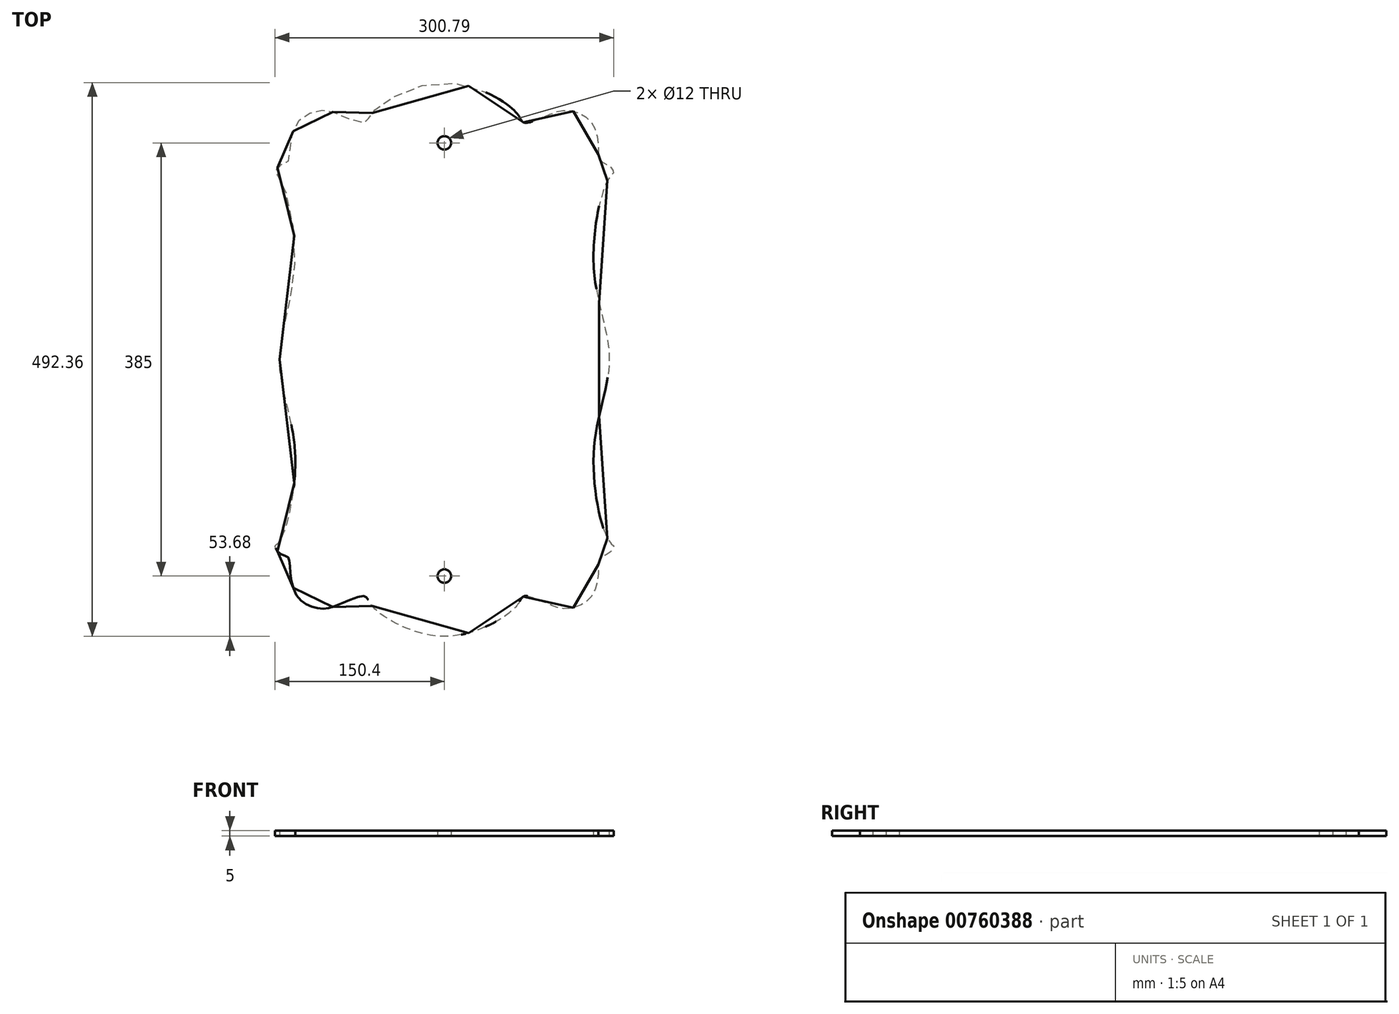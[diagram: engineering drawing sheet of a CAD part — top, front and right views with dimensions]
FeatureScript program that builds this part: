
annotation { "Feature Type Name" : "Feature", "Feature Type Description" : "" }
export const myFeature = defineFeature(function(context is Context, id is Id, definition is map)
    precondition{}
    {
        {
            var Q0;
            Q0=qCreatedBy(makeId("Top.planeOp"),FACE);
            var sketch = newSketch(context, id + "F0", { "sketchPlane" : qUnion([Q0])});
            skPoint(sketch, "E0", {"position": v(150.32, -165.76) * mm});
            skPoint(sketch, "E1", {"position": v(107.37, -221.56) * mm});
            skPoint(sketch, "E2", {"position": v(69.02, -211.72) * mm});
            skPoint(sketch, "E3", {"position": v(0, -246.18) * mm});
            skPoint(sketch, "E4", {"position": v(138.05, -177.25) * mm});
            skPoint(sketch, "E5", {"position": v(146.48, 0) * mm});
            skPoint(sketch, "E6", {"position": v(132.68, -82.88) * mm});
            skLineSegment(sketch, "E7", {"start": v(0, 292) * mm, "end": v(0, -246.18) * mm, "construction": true});
            skPoint(sketch, "E8.MirrorP", {"position": v(-146.48, 0) * mm});
            skPoint(sketch, "E9.MirrorP", {"position": v(-132.68, -82.88) * mm});
            skPoint(sketch, "E10.MirrorP", {"position": v(-150.32, -165.76) * mm});
            skPoint(sketch, "E11.MirrorP", {"position": v(-138.05, -177.25) * mm});
            skPoint(sketch, "E12.MirrorP", {"position": v(-107.37, -221.56) * mm});
            skPoint(sketch, "E13.MirrorP", {"position": v(-69.02, -211.72) * mm});
            skPoint(sketch, "E14", {"position": v(0, 0) * mm});
            skPoint(sketch, "E15", {"position": v(-146.25, -161.4) * mm});
            skPoint(sketch, "E16", {"position": v(-136.87, -189.28) * mm});
            skPoint(sketch, "E17", {"position": v(-146.26, -172.33) * mm});
            skPoint(sketch, "E18", {"position": v(-131.04, -210.06) * mm});
            skPoint(sketch, "E19", {"position": v(-94.82, -218.38) * mm});
            skPoint(sketch, "E20", {"position": v(-60.59, -222.84) * mm});
            skPoint(sketch, "E21", {"position": v(-67.25, -214.49) * mm});
            skPoint(sketch, "E22", {"position": v(-72.48, -210.2) * mm});
            skPoint(sketch, "E23", {"position": v(-119.37, -219.05) * mm});
            skPoint(sketch, "E24", {"position": v(-149.89, -167.68) * mm});
            skPoint(sketch, "E25.MirrorP", {"position": v(60.59, -222.84) * mm});
            skPoint(sketch, "E26.MirrorP", {"position": v(67.25, -214.49) * mm});
            skPoint(sketch, "E27.MirrorP", {"position": v(72.48, -210.2) * mm});
            skPoint(sketch, "E28.MirrorP", {"position": v(94.82, -218.38) * mm});
            skPoint(sketch, "E29.MirrorP", {"position": v(119.37, -219.05) * mm});
            skPoint(sketch, "E30.MirrorP", {"position": v(136.87, -189.28) * mm});
            skPoint(sketch, "E31.MirrorP", {"position": v(146.26, -172.33) * mm});
            skPoint(sketch, "E32.MirrorP", {"position": v(149.89, -167.68) * mm});
            skPoint(sketch, "E33.MirrorP", {"position": v(146.25, -161.4) * mm});
            skPoint(sketch, "E34", {"position": v(-139.73, -175.31) * mm});
            skPoint(sketch, "E35.MirrorP", {"position": v(131.04, -210.06) * mm});
            skPoint(sketch, "E36.MirrorP", {"position": v(-132.68, 82.88) * mm});
            skPoint(sketch, "E37.MirrorP", {"position": v(-139.73, 175.31) * mm});
            skPoint(sketch, "E38.MirrorP", {"position": v(-150.32, 165.76) * mm});
            skPoint(sketch, "E39.MirrorP", {"position": v(69.02, 211.72) * mm});
            skPoint(sketch, "E40.MirrorP", {"position": v(150.32, 165.76) * mm});
            skPoint(sketch, "E41.MirrorP", {"position": v(-67.25, 214.49) * mm});
            skPoint(sketch, "E42.MirrorP", {"position": v(131.04, 210.06) * mm});
            skPoint(sketch, "E43.MirrorP", {"position": v(60.59, 222.84) * mm});
            skPoint(sketch, "E44.MirrorP", {"position": v(119.37, 219.05) * mm});
            skPoint(sketch, "E45.MirrorP", {"position": v(136.87, 189.28) * mm});
            skPoint(sketch, "E46.MirrorP", {"position": v(-72.48, 210.2) * mm});
            skPoint(sketch, "E47.MirrorP", {"position": v(-138.05, 177.25) * mm});
            skPoint(sketch, "E48.MirrorP", {"position": v(-69.02, 211.72) * mm});
            skPoint(sketch, "E49.MirrorP", {"position": v(72.48, 210.2) * mm});
            skPoint(sketch, "E50.MirrorP", {"position": v(-146.25, 161.4) * mm});
            skPoint(sketch, "E51.MirrorP", {"position": v(-136.87, 189.28) * mm});
            skPoint(sketch, "E52.MirrorP", {"position": v(138.05, 177.25) * mm});
            skPoint(sketch, "E53.MirrorP", {"position": v(67.25, 214.49) * mm});
            skPoint(sketch, "E54.MirrorP", {"position": v(-149.89, 167.68) * mm});
            skPoint(sketch, "E55.MirrorP", {"position": v(149.89, 167.68) * mm});
            skPoint(sketch, "E56.MirrorP", {"position": v(-107.37, 221.56) * mm});
            skPoint(sketch, "E57.MirrorP", {"position": v(-94.82, 218.38) * mm});
            skPoint(sketch, "E58.MirrorP", {"position": v(146.26, 172.33) * mm});
            skPoint(sketch, "E59.MirrorP", {"position": v(107.37, 221.56) * mm});
            skPoint(sketch, "E60.MirrorP", {"position": v(-131.04, 210.06) * mm});
            skPoint(sketch, "E61.MirrorP", {"position": v(94.82, 218.38) * mm});
            skPoint(sketch, "E62.MirrorP", {"position": v(146.25, 161.4) * mm});
            skPoint(sketch, "E63.MirrorP", {"position": v(0, 246.18) * mm});
            skPoint(sketch, "E64.MirrorP", {"position": v(-146.26, 172.33) * mm});
            skPoint(sketch, "E65.MirrorP", {"position": v(-119.37, 219.05) * mm});
            skPoint(sketch, "E66.MirrorP", {"position": v(-60.59, 222.84) * mm});
            skPoint(sketch, "E67.MirrorP", {"position": v(132.68, 82.88) * mm});
            skFitSpline(sketch, "E68", {"points": [v(-146.48, 0) * mm, v(-132.68, 82.88) * mm, v(-146.25, 161.4) * mm, v(-150.32, 165.76) * mm, v(-149.89, 167.68) * mm, v(-146.26, 172.33) * mm, v(-139.73, 175.31) * mm, v(-138.05, 177.25) * mm, v(-136.87, 189.28) * mm, v(-131.04, 210.06) * mm, v(-119.37, 219.05) * mm, v(-107.37, 221.56) * mm, v(-94.82, 218.38) * mm, v(-72.48, 210.2) * mm, v(-69.02, 211.72) * mm, v(-67.25, 214.49) * mm, v(-60.59, 222.84) * mm, v(0, 246.18) * mm, v(60.59, 222.84) * mm, v(67.25, 214.49) * mm, v(69.02, 211.72) * mm, v(72.48, 210.2) * mm, v(94.82, 218.38) * mm, v(107.37, 221.56) * mm, v(119.37, 219.05) * mm, v(131.04, 210.06) * mm, v(136.87, 189.28) * mm, v(138.05, 177.25) * mm, v(146.26, 172.33) * mm, v(149.89, 167.68) * mm, v(150.32, 165.76) * mm, v(146.25, 161.4) * mm, v(132.68, 82.88) * mm, v(146.48, 0) * mm, v(132.68, -82.88) * mm, v(146.25, -161.4) * mm, v(150.32, -165.76) * mm, v(149.89, -167.68) * mm, v(146.26, -172.33) * mm, v(138.05, -177.25) * mm, v(136.87, -189.28) * mm, v(131.04, -210.06) * mm, v(119.37, -219.05) * mm, v(107.37, -221.56) * mm, v(94.82, -218.38) * mm, v(72.48, -210.2) * mm, v(69.02, -211.72) * mm, v(67.25, -214.49) * mm, v(60.59, -222.84) * mm, v(0, -246.18) * mm, v(-60.59, -222.84) * mm, v(-67.25, -214.49) * mm, v(-69.02, -211.72) * mm, v(-72.48, -210.2) * mm, v(-94.82, -218.38) * mm, v(-107.37, -221.56) * mm, v(-119.37, -219.05) * mm, v(-131.04, -210.06) * mm, v(-136.87, -189.28) * mm, v(-138.05, -177.25) * mm, v(-139.73, -175.31) * mm, v(-146.26, -172.33) * mm, v(-149.89, -167.68) * mm, v(-150.32, -165.76) * mm, v(-146.25, -161.4) * mm, v(-132.68, -82.88) * mm, v(-146.48, 0) * mm]});
            skPoint(sketch, "E69", {"position": v(0, 295) * mm});
            skPoint(sketch, "E70", {"position": v(-30, 295) * mm});
            skPoint(sketch, "E71", {"position": v(-225, 0) * mm});
            skPoint(sketch, "E72", {"position": v(-225, 100) * mm});
            skPoint(sketch, "E73.MirrorP", {"position": v(225, 100) * mm});
            skPoint(sketch, "E74.MirrorP", {"position": v(225, -60) * mm});
            skLineSegment(sketch, "E75", {"start": v(0, 0) * mm, "end": v(-373.3, 215.53) * mm, "construction": true});
            skLineSegment(sketch, "E76", {"start": v(0, 0) * mm, "end": v(-204.64, 354.44) * mm, "construction": true});
            skLineSegment(sketch, "E77", {"start": v(-225, 0) * mm, "end": v(-225, 100) * mm});
            skLineSegment(sketch, "E78", {"start": v(-30, 295) * mm, "end": v(0, 295) * mm});
            skPoint(sketch, "E79", {"position": v(-30, 100) * mm});
            skArc(sketch, "E80", {"start": v(-30, 295) * mm, "mid": v(-167.89, 237.89) * mm, "end": v(-225, 100) * mm});
            skLineSegment(sketch, "E81.MirrorCS", {"start": v(225, 0) * mm, "end": v(225, 100) * mm});
            skArc(sketch, "E82.MirrorCS", {"start": v(30, 295) * mm, "mid": v(167.89, 237.89) * mm, "end": v(225, 100) * mm});
            skLineSegment(sketch, "E83.MirrorCS", {"start": v(30, 295) * mm, "end": v(0, 295) * mm});
            skArc(sketch, "E84.MirrorCS", {"start": v(-30, -295) * mm, "mid": v(-167.89, -237.89) * mm, "end": v(-225, -100) * mm});
            skLineSegment(sketch, "E85.MirrorCS", {"start": v(-225, 0) * mm, "end": v(-225, -100) * mm});
            skLineSegment(sketch, "E86.MirrorCS", {"start": v(225, 0) * mm, "end": v(225, -100) * mm});
            skArc(sketch, "E87.MirrorCS", {"start": v(30, -295) * mm, "mid": v(167.89, -237.89) * mm, "end": v(225, -100) * mm});
            skLineSegment(sketch, "E88.MirrorCS", {"start": v(30, -295) * mm, "end": v(0, -295) * mm});
            skLineSegment(sketch, "E89.MirrorCS", {"start": v(-30, -295) * mm, "end": v(0, -295) * mm});
            skCircle(sketch, "E90", {"center": v(0, 192.5) * mm, "radius": 6 * mm});
            skCircle(sketch, "E91.MirrorC", {"center": v(0, -192.5) * mm, "radius": 6 * mm});
            skSolve(sketch);
        }
        {
            var Q0;
            Q0=makeQuery(id+"F0.imprint","IMPRINT",FACE,{"disambiguationData":[TD([[makeQuery(id+"F0.imprint","IMPRINT",EDGE,{"derivedFrom":sQuery(id+"F0.wireOp",EDGE,"E68")}),-1.0]])]});
            extrude(context, id + "F1", {"entities" : qUnion([Q0]), "endBound" : BoundingType.SYMMETRIC, "depth" : 5 * mm});
        }
        {
            var Q0;
            Q0=makeQuery(id+"F1.opExtrude","CAP_FACE",FACE,{"disambiguationData":[OSD([sQuery(id+"F0.wireOp",EDGE,"E68"),sQuery(id+"F0.wireOp",EDGE,"E90"),sQuery(id+"F0.wireOp",EDGE,"E91.MirrorC")])],"isStart":false});
            cPlane(context, id + "F2", {"entities" : qUnion([Q0]), "cplaneType" : CPlaneType.OFFSET, "offset" : 50 * mm, "width" : 150 * mm, "height" : 150 * mm});
        }
    });
